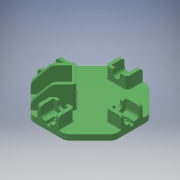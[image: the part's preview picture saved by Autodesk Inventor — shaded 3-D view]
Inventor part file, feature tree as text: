
AUTODESK INVENTOR PART (.ipt)
format: ipt  version: 2019 (Build 230136000, 136)  size: 662,528 bytes
history: native  units: mm
features: reference x13, extrude x9, fillet x8, other x8, sketch x6, pattern_circular x1, chamfer x1
ambient origin geometry x8: Origin, YZ Plane, XZ Plane, XY Plane, X Axis, Y Axis, Z Axis, Center Point
bodies: Solid1 (feature_tree)
feature tree (46):
  sketch  "Sketch1"  dims[d1=18.415mm d2=0.0mm d3=8.535mm d4=0.0mm]
  extrude  "Extrusion1"  Depth=8.535mm TaperAngle=0.0deg
  extrude  "Extrusion2"  Depth=0.1mm
  sketch  "Sketch5"  dims[d11=8.4441mm d12=0.0mm d13=11.4441mm]
  extrude  "Extrusion7"  Depth=12.4441mm TaperAngle=0.0deg
  sketch  "Sketch2"  dims[d5=0.2mm d6=0.1mm]
  extrude  "Extrusion3"  Depth=11.4441mm
  extrude  "Extrusion4"  Depth=18.6436mm
  extrude  "Extrusion5"  Depth=0.2mm
  extrude  "Extrusion6"  Depth=0.2mm
  pattern_circular  "Circular Pattern1"  [2 undecoded]
  extrude  "Extrusion8"  Depth=5.0mm
  extrude  "Extrusion9"  Depth=0.2mm
  fillet  "Fillet1"  Radius=13.415mm
  fillet  "Fillet2"  Radius=0.2mm
  chamfer  "Chamfer1"  Distance=10.0mm
  fillet  "Fillet3"  Radius=40.0mm
  fillet  "Fillet4"  Radius=5.4mm
  fillet  "Fillet5"  Radius=34.865mm
  fillet  "Fillet6"  Radius=0.4mm
  fillet  "Fillet7"  Radius=44.2436mm
  fillet  "Fillet8"  Radius=49.2436mm
  reference  "Reference13"
  reference  "Reference14"
  reference  "Reference15"
  reference  "Reference16"
  reference  "Reference17"
  sketch  "Sketch3"  dims[d7=19.6436mm d8=0.0mm d9=12.4441mm d10=0.0mm]
  reference  "Reference18"
  reference  "Reference19"
  reference  "Reference24"
  sketch  "Sketch6"  dims[d14=3.0mm d15=18.6436mm]
  reference  "Reference25"
  reference  "Reference26"
  reference  "Reference27"
  reference  "Reference28"
  sketch  "Sketch7"  dims[d16=0.2mm d17=0.2mm d18=0.2mm d19=0.2mm d20=5.0mm d21=0.2mm d22=13.415mm d23=0.2mm d24=10.0mm d25=0.0mm d26=40.0mm d27=360.0deg d29=5.4mm d30=34.865mm d31=0.0mm d32=0.4mm d33=44.2436mm d34=0.0mm d35=49.2436mm d36=2.9mm d38=48.844mm d39=0.0mm d40=12.5mm d41=4.5mm d42=23.243333mm d43=2.0mm d44=45.0deg d45=12.5mm d46=5.0mm d53=1.25mm d54=2.0mm d55=2.0mm d56=0.2mm]
  reference  "Reference29"
  other  "<userpath>\Documents\SE101\3D Models\Assembly.iam"
  other  "Assembly.iam"
  other  "Solarbotics-GM3:1"
  other  "GM3-driver_side-1:1"
  other  "GM3-encoder_side-1:1"
  other  "Solenoid:2"
  other  "Solenoid Body:1"
  other  "Solenoid Arm:1"
note: 2 required parameter values undecoded (feature->parameter linkage not recoverable at this tier; creation-order binding heuristic only, values carry confidence <= 0.55)
